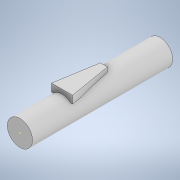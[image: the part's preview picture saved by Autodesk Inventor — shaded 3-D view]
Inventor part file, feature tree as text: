
AUTODESK INVENTOR PART (.ipt)
format: ipt  version: 2021 (Build 250183000, 183)  size: 112,640 bytes
history: native  units: in
note: dims shown in document units (in); Inventor stores cm internally (conversion verified against a paired STEP export)
features: sketch x3, extrude x2, plane x1
ambient origin geometry x8: Origin, YZ Plane, XZ Plane, XY Plane, X Axis, Y Axis, Z Axis, Center Point
bodies: Body1 (feature_tree)
feature tree (6):
  sketch  "Sketch4"  dims[d5=0.7087in d6=0.3543in]
  sketch  "Sketch5"  dims[d7=3.937in d8=0.1969in]
  plane  "Work Plane1"
  sketch  "Sketch6"  dims[d9=0.2953in d10=0.2953in d11=1.1811in d12=1.5748in d13=3.937in d14=0.0in d15=0.1181in d16=0.0in d17=0.0984in d18=0.0in]
  extrude  "Extrusion3"  Depth=0.3543in
  extrude  "Extrusion4"  Depth=3.937in
